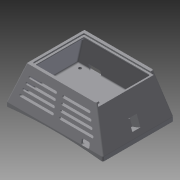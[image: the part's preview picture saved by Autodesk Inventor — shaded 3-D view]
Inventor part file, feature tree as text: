
AUTODESK INVENTOR PART (.ipt)
format: ipt  version: 2015 SP1 (Build 190203100, 203)  size: 479,744 bytes
history: native  units: in
note: dims shown in document units (in); Inventor stores cm internally (conversion verified against a paired STEP export)
features: extrude x11, other x6, mirror x4, projected_geometry x4, fillet x3, loft x2, imported_body x1, hole x1, plane x1, sketch x1
ambient origin geometry x8: Origin, YZ Plane, XZ Plane, XY Plane, X Axis, Y Axis, Z Axis, Center Point
bodies: Solid2 (feature_tree)
feature tree (34):
  imported_body  "Base"
  other  "Top Plane"
  other  "Top"
  loft  "Loft Outer"
  loft  "Loft Inner"
  extrude  "Bottom"  Depth=0.3937in
  other  "Front/Back Hole Pattern"
  extrude  "Board Curvature"  Depth=0.0787in
  hole  "Screw Hole"  [1 undecoded]
  mirror  "Screw Hole Mirror1"
  mirror  "Screw Hole Mirror2"
  other  "Switch Capture"
  extrude  "Switch Hole"  Depth=0.0787in
  extrude  "Switch Walls"  Depth=0.0787in
  plane  "Work Plane2"
  extrude  "Switch Wall Back"  Depth=0.0787in
  other  "Front/Back Lip"
  extrude  "Side Lip Clear"  Depth=0.7087in
  extrude  "Back Lip Retaining Lip"  Depth=0.0787in
  extrude  "Side  Lip Retaining Lip"  TaperAngle=0.0deg  [1 undecoded]
  mirror  "Front Lip"
  fillet  "Fillet Outer"  Radius=0.2756in
  fillet  "Fillet Inner"  Radius=7.4803in
  extrude  "Power Hole"  Depth=0.0787in TaperAngle=0.0deg
  extrude  "Vent Hole"  Depth=0.0787in
  mirror  "Vent Mirrored"
  extrude  "Output Hole"  Depth=0.0787in
  fillet  "Hole Fillet"  Radius=0.177in
  sketch  "Sketch4"  dims[d0=3.8976in d1=3.189in d2=0.7874in d3=0.3937in d4=3.1102in d5=2.0866in d6=0.5433in d7=0.4646in d8=2.7953in d9=0.7087in d14=2.1654in d21=0.0in d22=90.0deg d23=0.0in d24=90.0deg d25=0.2756in d26=0.0in d27=7.4803in d29=0.2756in d30=0.0in d32=0.0787in d33=0.2953in d34=0.177in d35=0.75in d36=0.375in d37=0.25in d38=0.5635in d39=1.0in d40=0.8108in d41=4.7244in d42=3.5433in d44=0.1181in d45=0.0787in d46=0.0787in d48=45.0deg d49=0.2756in d50=0.0in d53=0.2756in d54=0.0in d55=0.0945in d56=0.0in d57=90.0deg d58=0.0in d59=90.0deg d60=0.0787in d61=0.0787in d62=135.0deg d63=0.0787in d64=0.0787in d65=0.0787in d66=0.2756in d67=0.0in d68=0.4724in d69=0.315in d73=0.2756in d74=0.0in d75=0.315in d78=0.1378in d82=0.1378in d83=0.1969in d84=0.1378in d85=0.1969in d88=0.5512in d89=0.2756in d90=0.0in d91=0.315in d92=0.0787in d93=0.7087in d96=0.2756in d97=0.0in d98=0.7087in d99=0.7087in d102=0.4724in d103=0.6299in d104=0.5827in d105=0.7402in d106=0.0787in d107=0.3937in d108=0.0in d109=0.5039in d110=0.0in d111=0.0787in d112=0.0787in d113=0.0in d114=0.0787in]
  projected_geometry  "Projected Loop2"
  other  "Right Lip"
  projected_geometry  "Projected Loop3"
  projected_geometry  "Projected Loop4"
  projected_geometry  "Projected Loop5"
note: 2 required parameter values undecoded (feature->parameter linkage not recoverable at this tier; creation-order binding heuristic only, values carry confidence <= 0.55)
